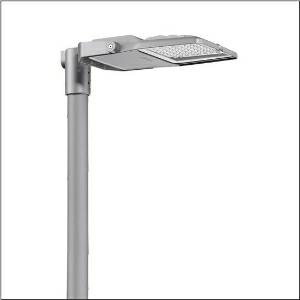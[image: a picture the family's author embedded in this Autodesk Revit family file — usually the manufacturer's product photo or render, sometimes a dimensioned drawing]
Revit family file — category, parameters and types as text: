
# Revit family: floodlight_fl_21_mini___pl61_5xa7776c2c3a_9e20
name_source: partatom
category: Lighting Fixtures
units: mm (PartAtom-declared; Revit-internal decimal feet)

## family parameters
Cut with Voids When Loaded = No
Host = Face
Light Source = No
Part Type = Normal
Room Calculation Point = No
Round Connector Dimension = Use Diameter
Shared = No

## types (1)
- --- (1 x LED, 11960 lm, 89 W, 3000K)
    Apparent Load = 89 VA
    CIE Flux Codes = 33 65 98 100 100
    Color Rendering = 70
    Color Temperature = 3000K
    Default Elevation = 1800 mm
    Description = Floodlight FL 21 mini, floodlight, primary light control with lens, of PMMA, primary optical cover: protective disc, of toughened safety glass, transparent, light distribution: PL61, light emission: direct distribution, installation type: surface-mounted, LED, High Power LED, rated luminous flux: 11.960lm, luminous efficacy: 134lm/W, light colour: 730, colour temperature: 3000K, control gear: Smart Interface (Zhaga), control: flexible luminous flux parameterisation, time-dependent luminous flux control, constant luminous flux control, overheat protection, pre-setting: logarithmic dimming characteristic, with terminal, 6-pole, mains connection: 220..240V, AC, 50/60Hz, start of lifetime: 89W, end of service life: 94W, reduction: 43W, luminaire housing, of diecast aluminium, powder-coated, SITECO metallic grey (DB 702S), corrosivity category C5 mid according to DIN EN ISO 12944, suitable for swimming pools, chlorine-resistant, sealing non-destructively replaceable, please order mast flange separately, mast bracket, of steel, galvanised, powder-coated, SITECO metallic grey (DB 702S), Smart Interface below and above, protection rating (complete): IP66, insulation class (complete): insulation class II (safety insulation), certification: CE, ENEC, VDE, protection symbol: D, impact resistance: IK08, permissible operating ambient temperature: -40..+40°C, permissible operating ambient temperature for outdoor applications: -40..+50°C, standard: DIN EN 12944, LABS conformity tested according to VDMA 24364:2018-05, packaging unit: 1 piece

Light Distribution: PL61
    Height = 70 mm
    Lamp = 1 x LED
    Lamp Light Flux = 11960 lm
    Lamp Power = 89 W
    Lamp count = 1
    Length = 485 mm
    Luminous efficacy = 134 lm/W
    Manufacturer = Siteco
    ModVariant = No
    Model = 5XA7776C2C3A
    Number of Poles = 1
    OnlyDefault = Yes
    Power Factor = 1
    Product Name = Floodlight FL 21 mini | PL61
    Product group = floodlight | pylon annexe
    ProductGroupID = 6201
    Protection Class = Protection class II
    Protection Degree = IP 66
    RLX_Detail_Level = 1
    RLX_Emergency_Light_Flux = 0 lm
    RLX_Emergency_Type = 0
    RLX_Emergency_Type_DB = No
    RlxData = <blob elided: 101045 chars, md5=bddf1c97>
    Socket = socket
    Standby Power = 0 W
    System Light Flux = 11960 lm
    System Power = 89 W
    Type Comments = factory setting: luminous flux: 100 % | dim-lin: 254 | 456 mA
    Type Image = l_1007125.jpg
    URL = http://relux.com
    VarID = @adj_171475
    Voltage = 0 V
    Weight = 0.00 kg
    Width = 337 mm

## geometry (parser evidence)
native form markers: Blend x4, Sweep x10
no freeform markers — native parametric forms only
